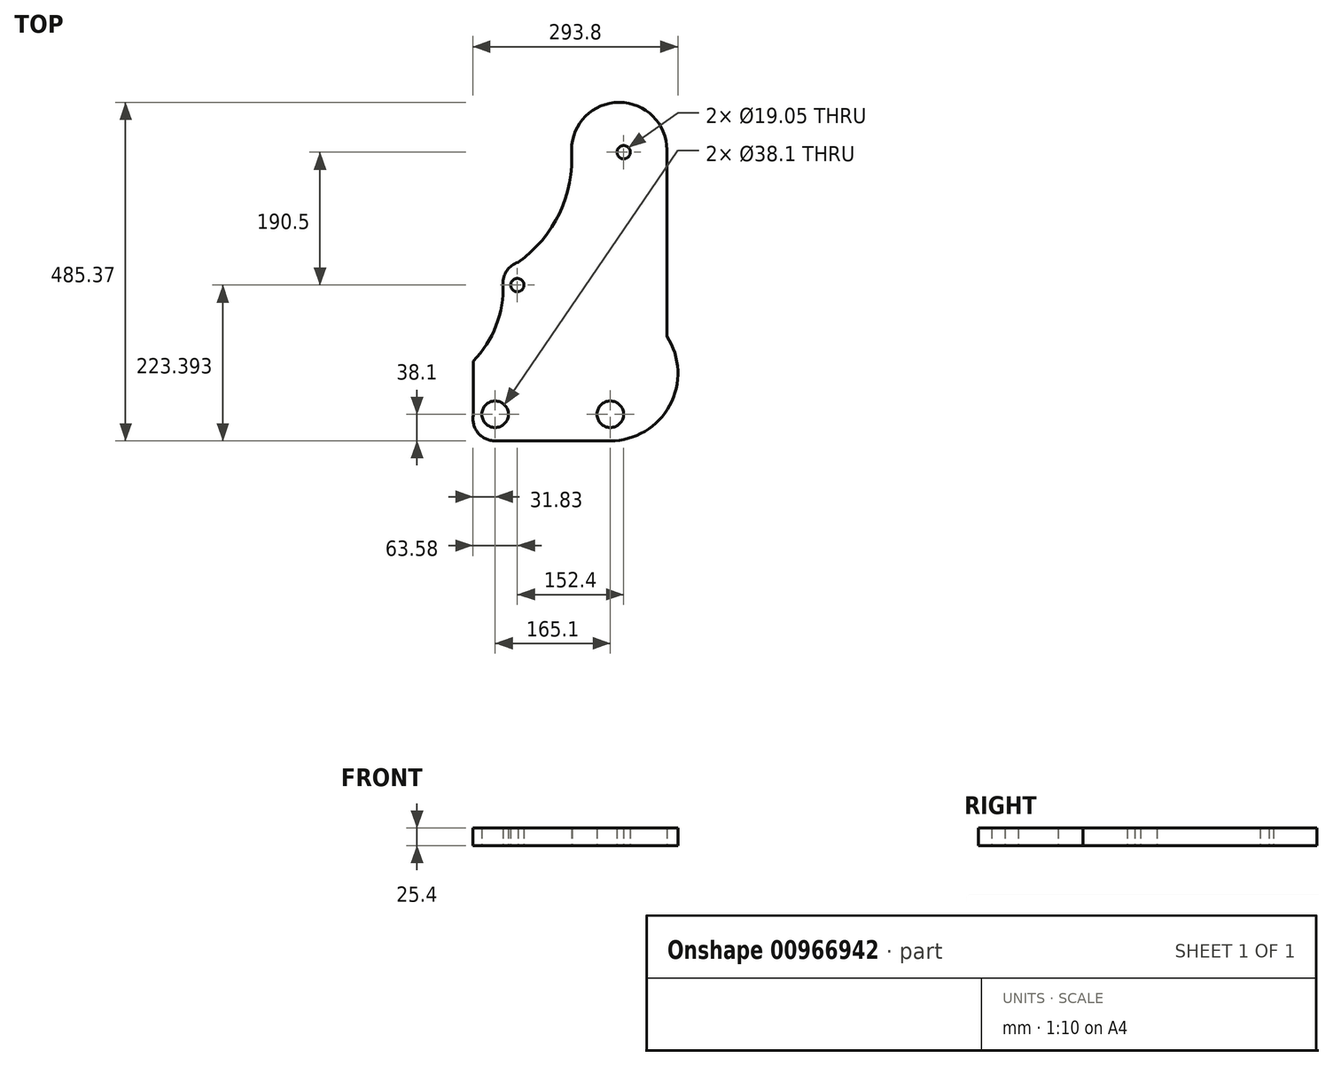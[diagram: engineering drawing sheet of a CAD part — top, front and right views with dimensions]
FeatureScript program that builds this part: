
annotation { "Feature Type Name" : "Feature", "Feature Type Description" : "" }
export const myFeature = defineFeature(function(context is Context, id is Id, definition is map)
    precondition{}
    {
        {
            var Q0;
            Q0=qCreatedBy(makeId("Top.planeOp"),FACE);
            var sketch = newSketch(context, id + "F0", { "sketchPlane" : qUnion([Q0])});
            skLineSegment(sketch, "E0", {"start": v(0, 0) * mm, "end": v(165.1, 0) * mm});
            skCircle(sketch, "E1", {"center": v(0, 0) * mm, "radius": 19.05 * mm});
            skCircle(sketch, "E2", {"center": v(165.1, 0) * mm, "radius": 19.05 * mm});
            skPoint(sketch, "E3", {"position": v(107.95, 0) * mm});
            skLineSegment(sketch, "E4", {"start": v(107.95, 0) * mm, "end": v(107.95, 147.2) * mm});
            skLineSegment(sketch, "E5", {"start": v(107.95, 147.2) * mm, "end": v(31.75, 147.2) * mm});
            skLineSegment(sketch, "E6", {"start": v(31.75, 147.2) * mm, "end": v(31.75, 185.3) * mm});
            skLineSegment(sketch, "E7", {"start": v(107.95, 147.2) * mm, "end": v(184.15, 147.2) * mm});
            skLineSegment(sketch, "E8", {"start": v(184.15, 147.2) * mm, "end": v(184.15, 375.8) * mm});
            skCircle(sketch, "E9", {"center": v(184.15, 375.8) * mm, "radius": 9.53 * mm});
            skCircle(sketch, "E10", {"center": v(31.75, 185.3) * mm, "radius": 9.52 * mm});
            skLineSegment(sketch, "E11", {"start": v(165.1, 0) * mm, "end": v(165.1, -38.1) * mm});
            skLineSegment(sketch, "E12", {"start": v(0, 0) * mm, "end": v(0, -38.1) * mm});
            skLineSegment(sketch, "E13", {"start": v(165.1, -38.1) * mm, "end": v(0, -38.1) * mm});
            skLineSegment(sketch, "E14", {"start": v(246.17, 111.78) * mm, "end": v(246.17, 379) * mm});
            skArc(sketch, "E15", {"start": v(246.17, 379) * mm, "mid": v(177.9, 447.27) * mm, "end": v(109.62, 379) * mm});
            skArc(sketch, "E16", {"start": v(33.11, 217.96) * mm, "mid": v(92.38, 288.5) * mm, "end": v(109.62, 379) * mm});
            skArc(sketch, "E17", {"start": v(-31.2, 0) * mm, "mid": v(-24.63, -26.44) * mm, "end": v(0, -38.1) * mm});
            skArc(sketch, "E18", {"start": v(165.1, -38.1) * mm, "mid": v(250.3, 12.68) * mm, "end": v(246.17, 111.78) * mm});
            skArc(sketch, "E19", {"start": v(33.11, 217.96) * mm, "mid": v(16.77, 206.02) * mm, "end": v(11.3, 186.53) * mm});
            skLineSegment(sketch, "E20", {"start": v(-31.2, 0) * mm, "end": v(-31.2, 76.2) * mm});
            skArc(sketch, "E21", {"start": v(-31.2, 76.2) * mm, "mid": v(1.33, 127.02) * mm, "end": v(11.3, 186.53) * mm});
            skSolve(sketch);
        }
        {
            var Q0;
            Q0=makeQuery(id+"F0.imprint","IMPRINT",FACE,{"disambiguationData":[TD([[makeQuery(id+"F0.imprint","IMPRINT",EDGE,{"derivedFrom":sQuery(id+"F0.wireOp",EDGE,"E9")}),-1.0]])]});
            var Q1;
            {var subQ8=sQuery(id+"F0.wireOp",EDGE,"E13");Q1=makeQuery(id+"F0.imprint","IMPRINT",FACE,{"disambiguationData":[TD([[makeQuery(id+"F0.imprint","IMPRINT",EDGE,{"derivedFrom":subQ8}),-1.0]])]});}
            extrude(context, id + "F1", {"entities" : qUnion([Q0, Q1]), "depth" : 25.4 * mm, "offsetDistance" : 25.4 * mm});
        }
    });
